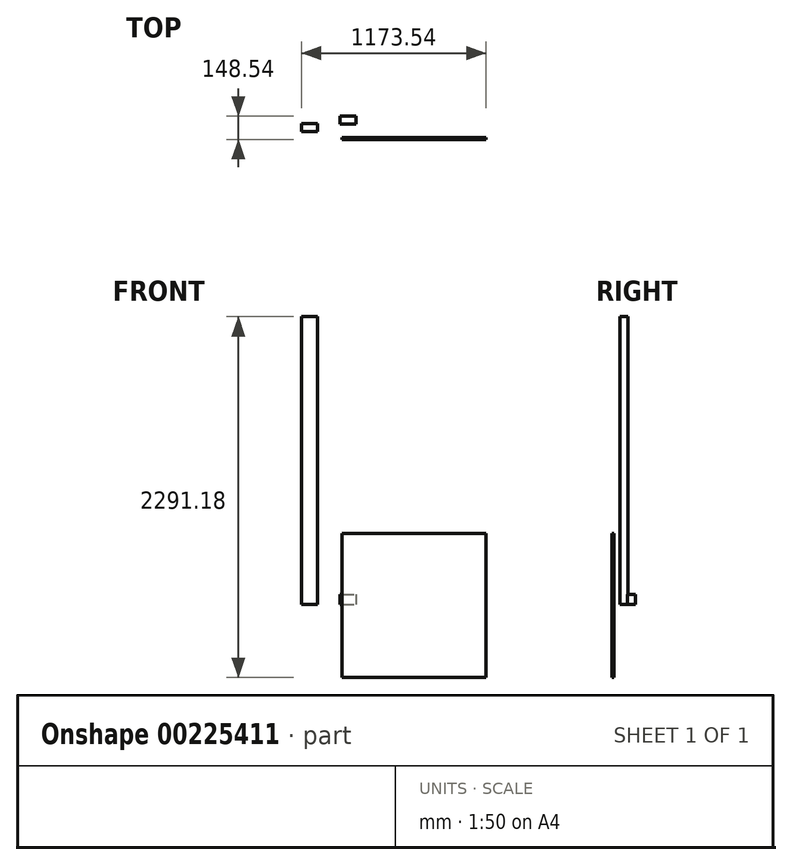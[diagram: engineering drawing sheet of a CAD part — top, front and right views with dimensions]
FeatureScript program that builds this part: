
annotation { "Feature Type Name" : "Feature", "Feature Type Description" : "" }
export const myFeature = defineFeature(function(context is Context, id is Id, definition is map)
    precondition{}
    {
        {
            var Q0;
            Q0=qCreatedBy(makeId("Top.planeOp"),FACE);
            var sketch = newSketch(context, id + "F0", { "sketchPlane" : qUnion([Q0])});
            skLineSegment(sketch, "E0.bottom", {"start": v(-145.74, 89.36) * mm, "end": v(-44.14, 89.36) * mm});
            skLineSegment(sketch, "E0.top", {"start": v(-145.74, 38.56) * mm, "end": v(-44.14, 38.56) * mm});
            skLineSegment(sketch, "E0.left", {"start": v(-145.74, 89.36) * mm, "end": v(-145.74, 38.56) * mm});
            skLineSegment(sketch, "E0.right", {"start": v(-44.14, 89.36) * mm, "end": v(-44.14, 38.56) * mm});
            skSolve(sketch);
        }
        {
            var Q0;
            Q0=makeQuery(id+"F0.imprint","IMPRINT",FACE,{"disambiguationData":[TD([[makeQuery(id+"F0.imprint","IMPRINT",EDGE,{"derivedFrom":sQuery(id+"F0.wireOp",EDGE,"E0.bottom")}),-1.0]])]});
            extrude(context, id + "F1", {"entities" : qUnion([Q0]), "depth" : 1828.8 * mm});
        }
        {
            var Q0;
            Q0=qCreatedBy(makeId("Front.planeOp"),FACE);
            var sketch = newSketch(context, id + "F2", { "sketchPlane" : qUnion([Q0])});
            skLineSegment(sketch, "E1.bottom", {"start": v(113.4, 452.02) * mm, "end": v(1027.8, 452.02) * mm});
            skLineSegment(sketch, "E1.top", {"start": v(113.4, -462.38) * mm, "end": v(1027.8, -462.38) * mm});
            skLineSegment(sketch, "E1.left", {"start": v(113.4, 452.02) * mm, "end": v(113.4, -462.38) * mm});
            skLineSegment(sketch, "E1.right", {"start": v(1027.8, 452.02) * mm, "end": v(1027.8, -462.38) * mm});
            skSolve(sketch);
        }
        {
            var Q0;
            Q0=makeQuery(id+"F2.imprint","IMPRINT",FACE,{"disambiguationData":[TD([[makeQuery(id+"F2.imprint","IMPRINT",EDGE,{"derivedFrom":sQuery(id+"F2.wireOp",EDGE,"E1.bottom")}),-1.0]])]});
            extrude(context, id + "F3", {"entities" : qUnion([Q0]), "depth" : 12.7 * mm});
        }
        {
            var Q0;
            Q0=qCreatedBy(makeId("Top.planeOp"),FACE);
            var sketch = newSketch(context, id + "F4", { "sketchPlane" : qUnion([Q0])});
            skLineSegment(sketch, "E2.bottom", {"start": v(100.8, 135.84) * mm, "end": v(202.4, 135.84) * mm});
            skLineSegment(sketch, "E2.top", {"start": v(100.8, 85.04) * mm, "end": v(202.4, 85.04) * mm});
            skLineSegment(sketch, "E2.left", {"start": v(100.8, 135.84) * mm, "end": v(100.8, 85.04) * mm});
            skLineSegment(sketch, "E2.right", {"start": v(202.4, 135.84) * mm, "end": v(202.4, 85.04) * mm});
            skSolve(sketch);
        }
        {
            var Q0;
            Q0=makeQuery(id+"F4.imprint","IMPRINT",FACE,{"disambiguationData":[TD([[makeQuery(id+"F4.imprint","IMPRINT",EDGE,{"derivedFrom":sQuery(id+"F4.wireOp",EDGE,"E2.bottom")}),-1.0]])]});
            extrude(context, id + "F5", {"entities" : qUnion([Q0]), "depth" : ((6 * 12) - 8) * mm});
        }
    });
